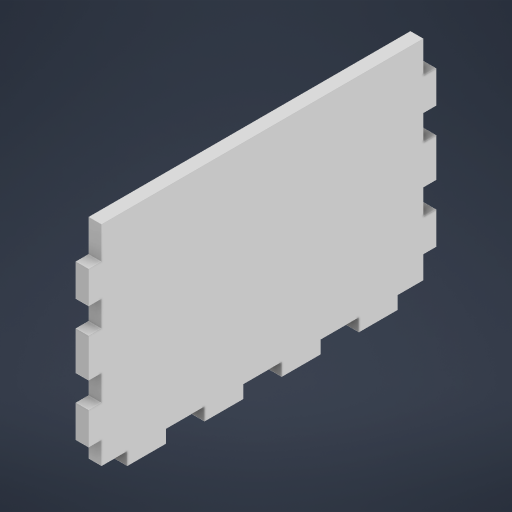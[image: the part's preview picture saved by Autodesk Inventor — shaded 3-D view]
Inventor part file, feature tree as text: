
AUTODESK INVENTOR PART (.ipt)
format: ipt  version: 2023.2 (Build 272271000, 271)  size: 286,720 bytes
history: native  units: mm
features: sketch x1
ambient origin geometry x8: Origin, YZ Plane, XZ Plane, XY Plane, X Axis, Y Axis, Z Axis, Center Point
bodies: Body1 (feature_tree)
feature tree (1):
  sketch  "Sketch1"  dims[d228=69.0mm d229=108.0mm d230=4.0mm d231=0.0mm d246=12.0mm d248=10.0mm d250=8.0mm d253=4.0mm d256=10.0mm d257=12.0mm d259=12.0mm d261=4.0mm d262=0.0mm d9=0.5mm d10=0.872665mm d11=0.5mm d12=0.872665mm d13=0.5mm d14=0.872665mm d27=0.5mm d28=0.872665mm d29=0.5mm d30=0.872665mm d88=0.5mm d89=0.872665mm d90=0.5mm d91=0.872665mm d116=0.5mm d117=0.872665mm d118=0.5mm d119=0.872665mm d154=0.5mm d155=0.872665mm d156=0.5mm d157=0.872665mm d181=0.5mm d182=0.872665mm d183=0.5mm d184=0.872665mm d221=0.5mm d222=0.872665mm d223=0.5mm d224=0.872665mm]
